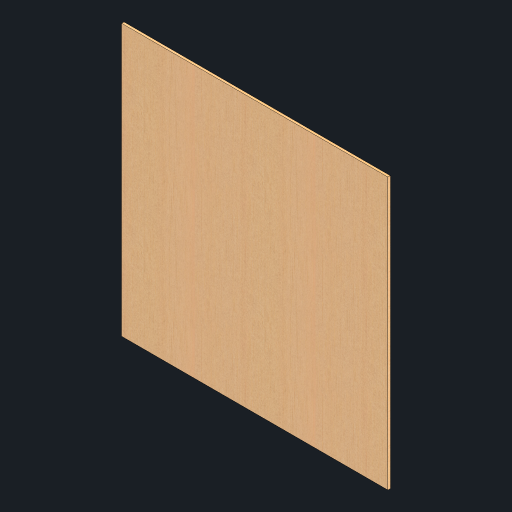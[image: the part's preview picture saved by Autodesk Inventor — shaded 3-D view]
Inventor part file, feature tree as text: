
AUTODESK INVENTOR PART (.ipt)
format: ipt  version: 2024.1 (Build 281209000, 209)  size: 244,224 bytes
history: native  units: mm
features: other x2, extrude x1, sketch x1
ambient origin geometry x8: Origin, YZ Plane, XZ Plane, XY Plane, X Axis, Y Axis, Z Axis, Center Point
bodies: Body1 (feature_tree)
feature tree (4):
  other  "솔리드1"
  extrude  "돌출1"  Depth=560.0mm
  sketch  "스케치1"
  other  "Finish1"
